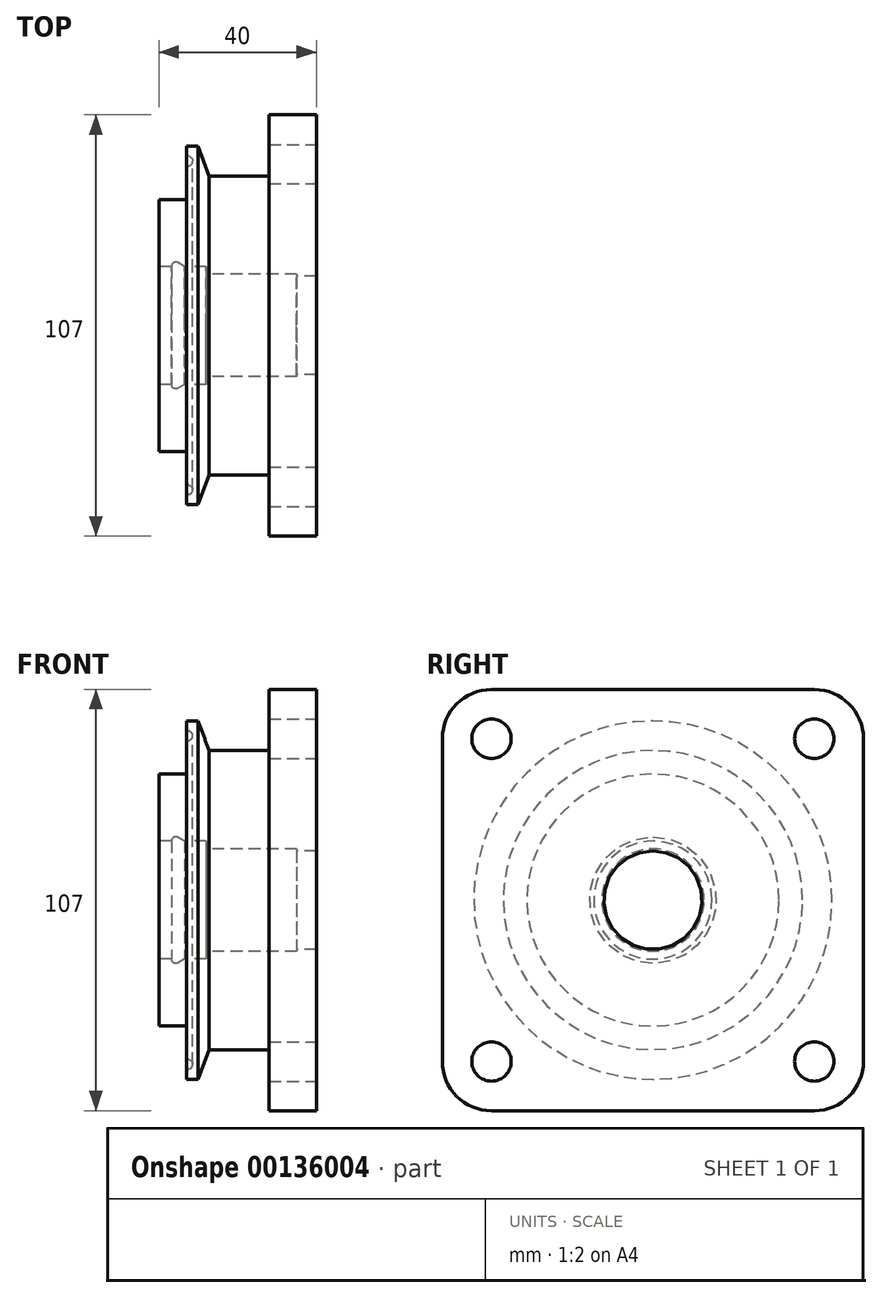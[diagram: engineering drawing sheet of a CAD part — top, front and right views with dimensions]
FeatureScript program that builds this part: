
annotation { "Feature Type Name" : "Feature", "Feature Type Description" : "" }
export const myFeature = defineFeature(function(context is Context, id is Id, definition is map)
    precondition{}
    {
        {
            var Q0;
            Q0=qCreatedBy(makeId("Front.planeOp"),FACE);
            var sketch = newSketch(context, id + "F0", { "sketchPlane" : qUnion([Q0])});
            skLineSegment(sketch, "E0", {"start": v(0, 32) * mm, "end": v(7, 32) * mm});
            skLineSegment(sketch, "E1", {"start": v(7, 32) * mm, "end": v(7, 39.75) * mm});
            skLineSegment(sketch, "E2", {"start": v(7, 45.5) * mm, "end": v(10, 45.5) * mm});
            skLineSegment(sketch, "E3", {"start": v(10, 45.5) * mm, "end": v(12.73, 38) * mm});
            skLineSegment(sketch, "E4", {"start": v(12.73, 38) * mm, "end": v(28, 38) * mm});
            skLineSegment(sketch, "E5", {"start": v(28, 38) * mm, "end": v(28, 0) * mm});
            skLineSegment(sketch, "E6", {"start": v(0, 0) * mm, "end": v(28, 0) * mm});
            skLineSegment(sketch, "E7", {"start": v(0, 32) * mm, "end": v(0, 0) * mm});
            skArc(sketch, "E8", {"start": v(7.87, 40.65) * mm, "mid": v(8.6, 41.75) * mm, "end": v(7.87, 42.85) * mm});
            skLineSegment(sketch, "E9", {"start": v(7.49, 43.02) * mm, "end": v(7.87, 42.85) * mm});
            skLineSegment(sketch, "E10", {"start": v(7.87, 40.65) * mm, "end": v(7.49, 40.48) * mm});
            skLineSegment(sketch, "E11", {"start": v(7.4, 41.75) * mm, "end": v(5.1, 41.75) * mm, "construction": true});
            skLineSegment(sketch, "E12.trimOffspring", {"start": v(7, 41.75) * mm, "end": v(7, 42.88) * mm});
            skLineSegment(sketch, "E13.trimOffspring", {"start": v(7, 43.75) * mm, "end": v(7, 45.5) * mm});
            skPoint(sketch, "E14.visualSharp", {"position": v(7, 43.22) * mm});
            skArc(sketch, "E14.filletArc", {"start": v(7, 43.75) * mm, "mid": v(7.13, 43.31) * mm, "end": v(7.49, 43.02) * mm});
            skPoint(sketch, "E15.visualSharp", {"position": v(7, 40.28) * mm});
            skArc(sketch, "E15.filletArc", {"start": v(7.49, 40.48) * mm, "mid": v(7.13, 40.19) * mm, "end": v(7, 39.75) * mm});
            skSolve(sketch);
        }
        {
            var Q0;
            Q0=qCreatedBy(makeId("Top.planeOp"),FACE);
            var sketch = newSketch(context, id + "F1", { "sketchPlane" : qUnion([Q0])});
            skLineSegment(sketch, "E16", {"start": v(-70.19, 0) * mm, "end": v(61.23, 0) * mm, "construction": true});
            skSolve(sketch);
        }
        {
            var Q0;
            Q0 = qSketchRegion(id + "F0", true);
            var Q1;
            Q1=sQuery(id+"F1.wireOp",EDGE,"E16");
            revolve(context, id + "F2", {"entities" : qUnion([Q0]), "axis" : qUnion([Q1]), "revolveType" : RevolveType.FULL});
        }
        {
            var Q0;
            Q0=makeQuery(id+"F2.opRevolve","SWEPT_FACE",FACE,{"disambiguationData":[OSD([sQuery(id+"F0.wireOp",EDGE,"E5")])]});
            var sketch = newSketch(context, id + "F3", { "sketchPlane" : qUnion([Q0])});
            skCircle(sketch, "E17", {"center": v(0, 0) * mm, "radius": 75 * mm});
            skSolve(sketch);
        }
        {
            var Q0;
            Q0 = qSketchRegion(id + "F3", true);
            extrude(context, id + "F4", {"entities" : qUnion([Q0]), "operationType" : NewBodyOperationType.ADD, "depth" : 12 * mm});
        }
        {
            var Q0;
            Q0=qCreatedBy(makeId("Front.planeOp"),FACE);
            var sketch = newSketch(context, id + "F5", { "sketchPlane" : qUnion([Q0])});
            skLineSegment(sketch, "E18", {"start": v(0, 15) * mm, "end": v(3.2, 15) * mm});
            skArc(sketch, "E19", {"start": v(4.85, 15.95) * mm, "mid": v(3.75, 15.95) * mm, "end": v(3.2, 15) * mm});
            skLineSegment(sketch, "E20", {"start": v(6.5, 15) * mm, "end": v(12, 15) * mm});
            skLineSegment(sketch, "E21", {"start": v(6.5, 15) * mm, "end": v(4.85, 15.95) * mm});
            skLineSegment(sketch, "E22", {"start": v(12, 15) * mm, "end": v(12, 13) * mm});
            skLineSegment(sketch, "E23", {"start": v(12, 13) * mm, "end": v(35, 13) * mm});
            skLineSegment(sketch, "E24", {"start": v(35, 13) * mm, "end": v(35, 12.5) * mm});
            skLineSegment(sketch, "E25", {"start": v(35, 12.5) * mm, "end": v(40, 12.5) * mm});
            skLineSegment(sketch, "E26", {"start": v(40, 12.5) * mm, "end": v(40, 0) * mm});
            skLineSegment(sketch, "E27", {"start": v(40, 0) * mm, "end": v(0, 0) * mm});
            skLineSegment(sketch, "E28", {"start": v(0, 0) * mm, "end": v(0, 15) * mm});
            skSolve(sketch);
        }
        {
            var Q0;
            Q0 = qSketchRegion(id + "F5", true);
            var Q1;
            Q1=sQuery(id+"F5.wireOp",EDGE,"E27");
            revolve(context, id + "F6", {"operationType" : NewBodyOperationType.REMOVE, "entities" : qUnion([Q0]), "axis" : qUnion([Q1]), "revolveType" : RevolveType.FULL, "oppositeDirection" : true});
        }
        {
            var Q0;
            Q0=makeQuery(id+"F4.opExtrude","CAP_FACE",FACE,{"disambiguationData":[OSD([sQuery(id+"F3.wireOp",EDGE,"E17")])],"isStart":false});
            var sketch = newSketch(context, id + "F7", { "sketchPlane" : qUnion([Q0])});
            skLineSegment(sketch, "E29.bottom", {"start": v(41, 41) * mm, "end": v(-41, 41) * mm, "construction": true});
            skLineSegment(sketch, "E29.top", {"start": v(41, -41) * mm, "end": v(-41, -41) * mm, "construction": true});
            skLineSegment(sketch, "E29.left", {"start": v(41, 41) * mm, "end": v(41, -41) * mm, "construction": true});
            skLineSegment(sketch, "E29.right", {"start": v(-41, 41) * mm, "end": v(-41, -41) * mm, "construction": true});
            skPoint(sketch, "E29.middle", {"position": v(0, 0) * mm});
            skPoint(sketch, "E30", {"position": v(-41, 41) * mm});
            skPoint(sketch, "E31", {"position": v(41, 41) * mm});
            skPoint(sketch, "E32", {"position": v(41, -41) * mm});
            skPoint(sketch, "E33", {"position": v(-41, -41) * mm});
            skSolve(sketch);
        }
        {
            var Q0;
            Q0=sQuery(id+"F7.wireOp",VERTEX,"E30");
            var Q1;
            Q1=sQuery(id+"F7.wireOp",VERTEX,"E31");
            var Q2;
            Q2=sQuery(id+"F7.wireOp",VERTEX,"E32");
            var Q3;
            Q3=sQuery(id+"F7.wireOp",VERTEX,"E33");
            var Q4;
            Q4=makeQuery(id+"F2.opRevolve","SWEPT_BODY",BODY,{"disambiguationData":[OSD([sQuery(id+"F0.wireOp",EDGE,"E0"),sQuery(id+"F0.wireOp",EDGE,"E1"),sQuery(id+"F0.wireOp",EDGE,"E2"),sQuery(id+"F0.wireOp",EDGE,"E3"),sQuery(id+"F0.wireOp",EDGE,"E4"),sQuery(id+"F0.wireOp",EDGE,"E5"),sQuery(id+"F0.wireOp",EDGE,"E6"),sQuery(id+"F0.wireOp",EDGE,"E7"),sQuery(id+"F0.wireOp",EDGE,"E8"),sQuery(id+"F0.wireOp",EDGE,"E9"),sQuery(id+"F0.wireOp",EDGE,"E10"),sQuery(id+"F0.wireOp",EDGE,"E13.trimOffspring"),sQuery(id+"F0.wireOp",EDGE,"E14.filletArc"),sQuery(id+"F0.wireOp",EDGE,"E15.filletArc")])]});
            hole(context, id + "F8", {"style" : HoleStyle.SIMPLE, "endStyle" : HoleEndStyle.THROUGH, "standardTappedOrClearance" : lookupTablePath({ "standard" : "ISO", "size" : "10", "type" : "Drilled" }), "standardBlindInLast" : lookupTablePath({ "standard" : "ISO", "size" : "10", "type" : "Drilled" }), "holeDiameter" : 10 * mm, "locations" : qUnion([Q0, Q1, Q2, Q3]), "scope" : qUnion([Q4]), "isTappedThrough" : true});
        }
        {
            var Q0;
            Q0=makeQuery(id+"F4.opExtrude","CAP_FACE",FACE,{"disambiguationData":[OSD([sQuery(id+"F3.wireOp",EDGE,"E17")])],"isStart":false});
            var sketch = newSketch(context, id + "F9", { "sketchPlane" : qUnion([Q0])});
            skLineSegment(sketch, "E34.bottom", {"start": v(41, 53.5) * mm, "end": v(-41, 53.5) * mm});
            skLineSegment(sketch, "E34.top", {"start": v(41, -53.5) * mm, "end": v(-41, -53.5) * mm});
            skLineSegment(sketch, "E34.left", {"start": v(53.5, 41) * mm, "end": v(53.5, -41) * mm});
            skLineSegment(sketch, "E34.right", {"start": v(-53.5, 41) * mm, "end": v(-53.5, -41) * mm});
            skPoint(sketch, "E34.middle", {"position": v(0, 0) * mm});
            skPoint(sketch, "E35.visualSharp", {"position": v(-53.5, 53.5) * mm});
            skArc(sketch, "E35.filletArc", {"start": v(-41, 53.5) * mm, "mid": v(-49.84, 49.84) * mm, "end": v(-53.5, 41) * mm});
            skPoint(sketch, "E36.visualSharp", {"position": v(-53.5, -53.5) * mm});
            skArc(sketch, "E36.filletArc", {"start": v(-53.5, -41) * mm, "mid": v(-49.84, -49.84) * mm, "end": v(-41, -53.5) * mm});
            skPoint(sketch, "E37.visualSharp", {"position": v(53.5, -53.5) * mm});
            skArc(sketch, "E37.filletArc", {"start": v(41, -53.5) * mm, "mid": v(49.84, -49.84) * mm, "end": v(53.5, -41) * mm});
            skPoint(sketch, "E38.visualSharp", {"position": v(53.5, 53.5) * mm});
            skArc(sketch, "E38.filletArc", {"start": v(53.5, 41) * mm, "mid": v(49.84, 49.84) * mm, "end": v(41, 53.5) * mm});
            skLineSegment(sketch, "E39.bottom", {"start": v(96.88, 82.61) * mm, "end": v(-96.88, 82.61) * mm});
            skLineSegment(sketch, "E39.top", {"start": v(96.88, -82.61) * mm, "end": v(-96.88, -82.61) * mm});
            skLineSegment(sketch, "E39.left", {"start": v(96.88, 82.61) * mm, "end": v(96.88, -82.61) * mm});
            skLineSegment(sketch, "E39.right", {"start": v(-96.88, 82.61) * mm, "end": v(-96.88, -82.61) * mm});
            skSolve(sketch);
        }
        {
            var Q0;
            Q0 = qSketchRegion(id + "F9", true);
            extrude(context, id + "F10", {"entities" : qUnion([Q0]), "operationType" : NewBodyOperationType.REMOVE, "oppositeDirection" : true, "depth" : 16 * mm});
        }
    });
